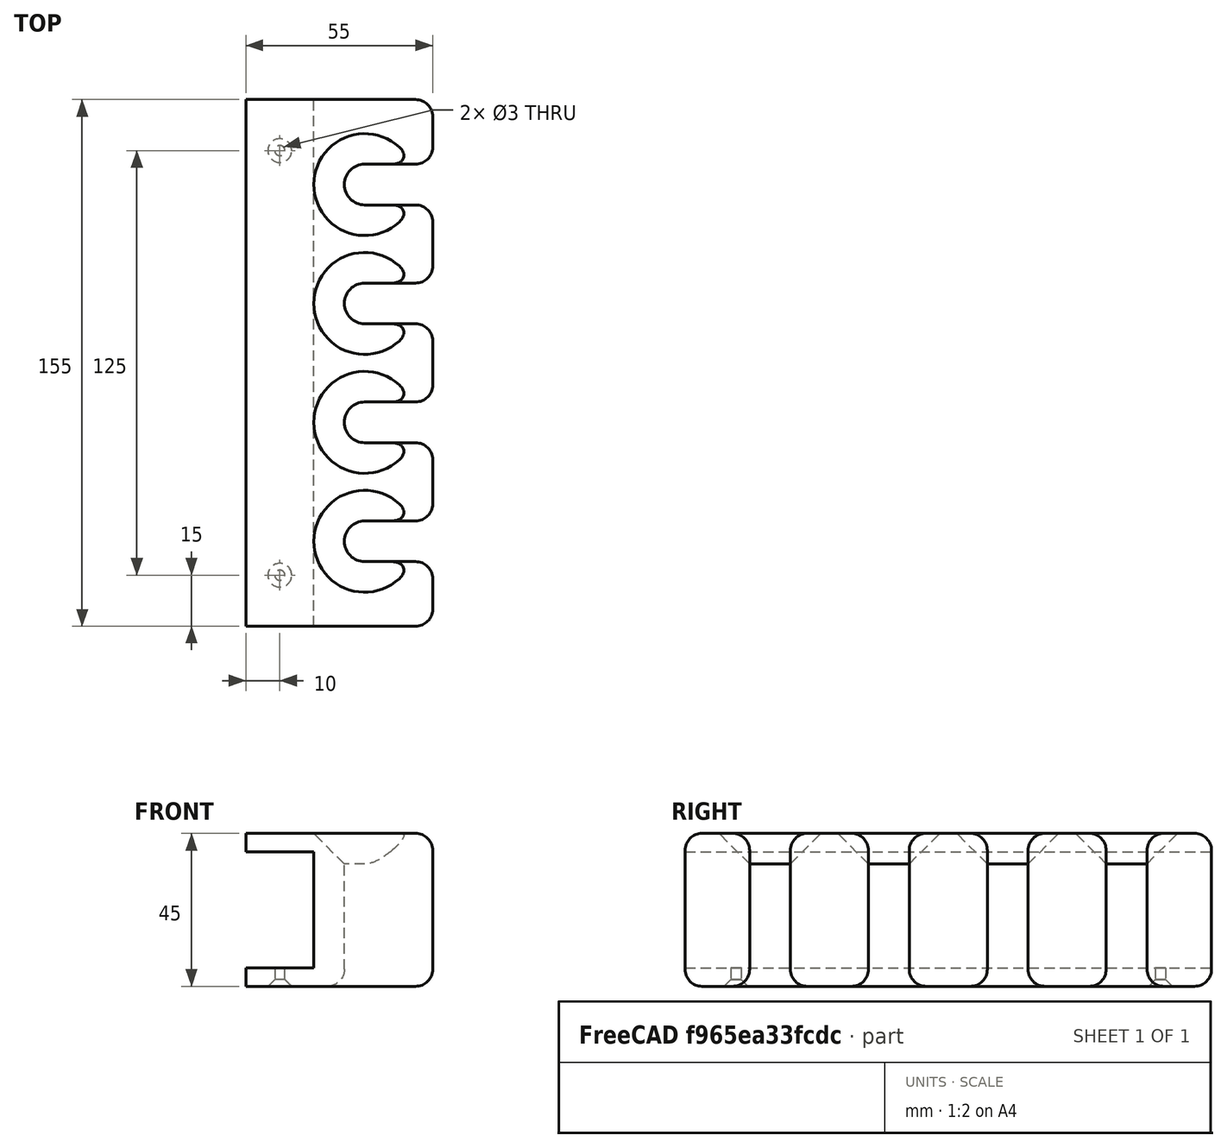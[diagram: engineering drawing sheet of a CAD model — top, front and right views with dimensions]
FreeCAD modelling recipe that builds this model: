
FCSTD DOCUMENT  (FreeCAD 0.21R33668 +7 (Git))
Label: ProbeHolderTable
License: All rights reserved
LicenseURL: http://en.wikipedia.org/wiki/All_rights_reserved
objects: PartDesign::Pocket×5, Sketcher::SketchObject×4, PartDesign::AdditiveBox×1, PartDesign::Fillet×1, PartDesign::Body×1, App::Part×1, Mesh::Feature×1
note: 19 computed .brp shape members not serialized (recipe doc carries the construction recipe); baked Part::Feature solids carry a one-line shape summary decoded from their .brp

FEATURE [PartDesign::AdditiveBox] Box
  AttacherType = Attacher::AttachEngine3D
  Height = 45
  Length = 55
  Width = 155
FEATURE [Sketcher::SketchObject] Sketch  label="ProbeSinkSchemaSketch"
  ExternalGeometry = -> [Box]
  FullyConstrained = true
  MapMode = 5
  Placement = pos=(0,0,45) rot=(0,0,1;0rad)
  Support = -> [Box]
  sketch-geometry (6):
    g0: LineSegment StartX=35 StartY=155 StartZ=0 EndX=35 EndY=0 EndZ=0
    g1: GeomPoint X=35 Y=77.5 Z=0
    g2: Circle CenterX=35 CenterY=130 CenterZ=0 NormalX=0 NormalY=0 NormalZ=1 AngleXU=0 Radius=15
    g3: Circle CenterX=35 CenterY=95 CenterZ=0 NormalX=0 NormalY=0 NormalZ=1 AngleXU=0 Radius=15
    g4: Circle CenterX=35 CenterY=60 CenterZ=0 NormalX=0 NormalY=0 NormalZ=1 AngleXU=0 Radius=15
    g5: Circle CenterX=35 CenterY=25 CenterZ=0 NormalX=0 NormalY=0 NormalZ=1 AngleXU=0 Radius=15
  constraints (17):
    c: PointOnObject(g0,g-1)
    c: Horizontal(g0,g-4)
    c: Symmetric(g0,g0,g1)
    c: PointOnObject(g2,g0)
    c: PointOnObject(g3,g0)
    c: PointOnObject(g4,g0)
    c: PointOnObject(g5,g0)
    c: Equal(g2,g3)
    c: Equal(g2,g4)
    c: Equal(g2,g5)
    c: Diameter(g2) = 30
    c: DistanceY(g3,g2) = 35
    c: DistanceY(g4,g3) = 35
    c: DistanceY(g5,g4) = 35
    c: DistanceY(g4,g1) = 17.5
    c: DistanceX(g0,g-4) = 20
    c: Vertical(g0)
FEATURE [PartDesign::Pocket] Pocket  label="ProbeSink"
  BaseFeature = -> Box
  Direction = (0,0,-1)
  Length = 9
  Length2 = 5
  Profile = -> Sketch
  ReferenceAxis = -> Sketch [N_Axis]
  TaperAngle = -45
  Type = 0
FEATURE [Sketcher::SketchObject] Sketch001  label="FrontPocketSchema"
  ExternalGeometry = -> [Pocket]
  FullyConstrained = true
  MapMode = 5
  Placement = pos=(0,0,45) rot=(0,0,1;0rad)
  Support = -> [Pocket]
  sketch-geometry (16):
    g0: ArcOfCircle CenterX=35 CenterY=130 CenterZ=0 NormalX=0 NormalY=0 NormalZ=1 AngleXU=0 Radius=6 StartAngle=1.5708 EndAngle=4.71239
    g1: LineSegment StartX=35 StartY=136 StartZ=0 EndX=55 EndY=136 EndZ=0
    g2: LineSegment StartX=35 StartY=124 StartZ=0 EndX=55 EndY=124 EndZ=0
    g3: LineSegment StartX=55 StartY=136 StartZ=0 EndX=55 EndY=124 EndZ=0
    g4: ArcOfCircle CenterX=35 CenterY=95 CenterZ=0 NormalX=0 NormalY=0 NormalZ=1 AngleXU=0 Radius=6 StartAngle=1.5708 EndAngle=4.71239
    g5: LineSegment StartX=35 StartY=101 StartZ=0 EndX=55 EndY=101 EndZ=0
    g6: LineSegment StartX=35 StartY=89 StartZ=0 EndX=55 EndY=89 EndZ=0
    g7: LineSegment StartX=55 StartY=101 StartZ=0 EndX=55 EndY=89 EndZ=0
    g8: ArcOfCircle CenterX=35 CenterY=60 CenterZ=0 NormalX=0 NormalY=0 NormalZ=1 AngleXU=0 Radius=6 StartAngle=1.5708 EndAngle=4.71239
    g9: LineSegment StartX=35 StartY=66 StartZ=0 EndX=55 EndY=66 EndZ=0
    g10: LineSegment StartX=35 StartY=54 StartZ=0 EndX=55 EndY=54 EndZ=0
    g11: LineSegment StartX=55 StartY=66 StartZ=0 EndX=55 EndY=54 EndZ=0
    g12: ArcOfCircle CenterX=35 CenterY=25 CenterZ=0 NormalX=0 NormalY=0 NormalZ=1 AngleXU=0 Radius=6 StartAngle=1.5708 EndAngle=4.71239
    g13: LineSegment StartX=35 StartY=31 StartZ=0 EndX=55 EndY=31 EndZ=0
    g14: LineSegment StartX=35 StartY=19 StartZ=0 EndX=55 EndY=19 EndZ=0
    g15: LineSegment StartX=55 StartY=31 StartZ=0 EndX=55 EndY=19 EndZ=0
  constraints (48):
    c: Coincident(g0,g-3)
    c: PointOnObject(g0,g-3)
    c: Vertical(g0,g0)
    c: Coincident(g1,g0)
    c: PointOnObject(g1,g-7)
    c: Horizontal(g1)
    c: Coincident(g2,g0)
    c: PointOnObject(g2,g-7)
    c: Horizontal(g2)
    c: Coincident(g3,g1)
    c: Coincident(g3,g2)
    c: Vertical(g0,g0)
    c: Coincident(g4,g-4)
    c: PointOnObject(g4,g-4)
    c: Vertical(g4,g4)
    c: Vertical(g4,g4)
    c: Coincident(g5,g4)
    c: PointOnObject(g5,g-7)
    c: Horizontal(g5)
    c: Coincident(g6,g4)
    c: PointOnObject(g6,g-7)
    c: Horizontal(g6)
    c: Coincident(g7,g5)
    c: Coincident(g7,g6)
    c: Coincident(g8,g-5)
    c: PointOnObject(g8,g-5)
    c: Vertical(g8,g8)
    c: Vertical(g8,g8)
    c: Coincident(g9,g8)
    c: PointOnObject(g9,g-7)
    c: Horizontal(g9)
    c: Coincident(g10,g8)
    c: PointOnObject(g10,g-7)
    c: Horizontal(g10)
    c: Coincident(g11,g9)
    c: Coincident(g11,g10)
    c: Coincident(g12,g-6)
    c: PointOnObject(g12,g-6)
    c: Vertical(g12,g12)
    c: Vertical(g12,g12)
    c: Coincident(g13,g12)
    c: PointOnObject(g13,g-7)
    c: Horizontal(g13)
    c: Coincident(g14,g12)
    c: PointOnObject(g14,g-7)
    c: Horizontal(g14)
    c: Coincident(g15,g13)
    c: Coincident(g15,g14)
FEATURE [PartDesign::Pocket] Pocket001  label="FrontPocket"
  BaseFeature = -> Pocket
  Direction = (0,0,-1)
  Length = 5
  Length2 = 5
  Profile = -> Sketch001
  ReferenceAxis = -> Sketch001 [N_Axis]
  Type = 1
FEATURE [Sketcher::SketchObject] Sketch002  label="TableSlotSchema"
  ExternalGeometry = -> [Pocket001]
  FullyConstrained = true
  MapMode = 5
  Placement = pos=(0,0,0) rot=(1,0,0;1.5708rad)
  Support = -> [Pocket001]
  sketch-geometry (6):
    g0: LineSegment StartX=0 StartY=5.4 StartZ=0 EndX=20 EndY=5.4 EndZ=0
    g1: LineSegment StartX=20 StartY=5.4 StartZ=0 EndX=20 EndY=39.6 EndZ=0
    g2: LineSegment StartX=20 StartY=39.6 StartZ=0 EndX=0 EndY=39.6 EndZ=0
    g3: LineSegment StartX=0 StartY=39.6 StartZ=0 EndX=0 EndY=5.4 EndZ=0
    g4: LineSegment StartX=0 StartY=45 StartZ=0 EndX=0 EndY=39.6 EndZ=0
    g5: LineSegment StartX=0 StartY=5.4 StartZ=0 EndX=0 EndY=0 EndZ=0
  constraints (16):
    c: Coincident(g0,g1)
    c: Coincident(g1,g2)
    c: Coincident(g2,g3)
    c: Coincident(g3,g0)
    c: Horizontal(g0)
    c: Horizontal(g2)
    c: Vertical(g1)
    c: Vertical(g3)
    c: PointOnObject(g0,g-2)
    c: DistanceY(g0,g2) = 34.2
    c: Coincident(g4,g-3)
    c: Coincident(g4,g2)
    c: Coincident(g5,g0)
    c: Coincident(g5,g-1)
    c: Equal(g4,g5)
    c: DistanceX(g2,g2) = 20
FEATURE [PartDesign::Pocket] Pocket002  label="TableSlot"
  BaseFeature = -> Pocket001
  Direction = (0,1,-2e-16)
  Length = 5
  Length2 = 5
  Profile = -> Sketch002
  ReferenceAxis = -> Sketch002 [N_Axis]
  Type = 1
FEATURE [Sketcher::SketchObject] Sketch003  label="ScrewHoleSchema"
  ExternalGeometry = -> [Pocket002]
  FullyConstrained = true
  MapMode = 5
  Placement = pos=(0,0,0) rot=(1,0,0;3.14159rad)
  Support = -> [Pocket002]
  sketch-geometry (4):
    g0: Circle CenterX=10 CenterY=-15 CenterZ=0 NormalX=0 NormalY=0 NormalZ=1 AngleXU=0 Radius=3.5
    g1: Circle CenterX=10 CenterY=-140 CenterZ=0 NormalX=0 NormalY=0 NormalZ=1 AngleXU=0 Radius=3.5
    g2: LineSegment StartX=0 StartY=-155 StartZ=0 EndX=10 EndY=-140 EndZ=0
    g3: LineSegment StartX=10 StartY=-15 StartZ=0 EndX=0 EndY=0 EndZ=0
  constraints (10):
    c: Vertical(g0,g1)
    c: Coincident(g2,g-3)
    c: Coincident(g2,g1)
    c: Coincident(g3,g0)
    c: Coincident(g3,g-1)
    c: Equal(g0,g1)
    c: Equal(g3,g2)
    c: DistanceX(g3,g0) = 10
    c: DistanceY(g0,g3) = 15
    c: Diameter(g0) = 7
FEATURE [PartDesign::Pocket] Pocket003  label="ScrewHeadPocket"
  BaseFeature = -> Pocket002
  Direction = (0,0,1)
  Length = 2
  Length2 = 5
  Profile = -> Sketch003
  ReferenceAxis = -> Sketch003 [N_Axis]
  TaperAngle = 45
  Type = 0
FEATURE [PartDesign::Pocket] Pocket004  label="ScrewShaftPocket"
  BaseFeature = -> Pocket003
  Direction = (0,0,-1)
  Length = 4
  Length2 = 5
  Profile = -> Pocket003 [Edge90,Edge88]
  Reversed = true
  Type = 0
FEATURE [PartDesign::Fillet] Fillet
  Base = -> Pocket004 [Edge24,Edge32,Edge37,Edge29,Edge21,Edge11,Edge22,Edge28,Edge36,Edge33,Edge25,Edge6,Edge5,Edge41,Edge42,Edge55,Edge81,Edge84,Edge51,Edge89,Edge86,Edge47,Edge75,Edge72,Edge43,Edge66,Edge17,Edge16,Edge58,Edge56,Edge54,Edge52,Edge50,Edge48,Edge46,Edge44]
  BaseFeature = -> Pocket004
  Radius = 5
  SupportTransform = false
  UseAllEdges = false
FEATURE [PartDesign::Body] Body  label="ProbeHolderBody"
  Group = -> [Box,Sketch,Pocket,Sketch001,Pocket001,Sketch002,Pocket002,Sketch003,Pocket003,Pocket004,Fillet]
  Origin = -> Origin001
  Tip = -> Fillet
FEATURE [App::Part] Part  label="ProbeHolderPart"
  Group = -> [Body]
  Origin = -> Origin
FEATURE [Mesh::Feature] Mesh  label="ProbeHolderPart (Meshed)"
